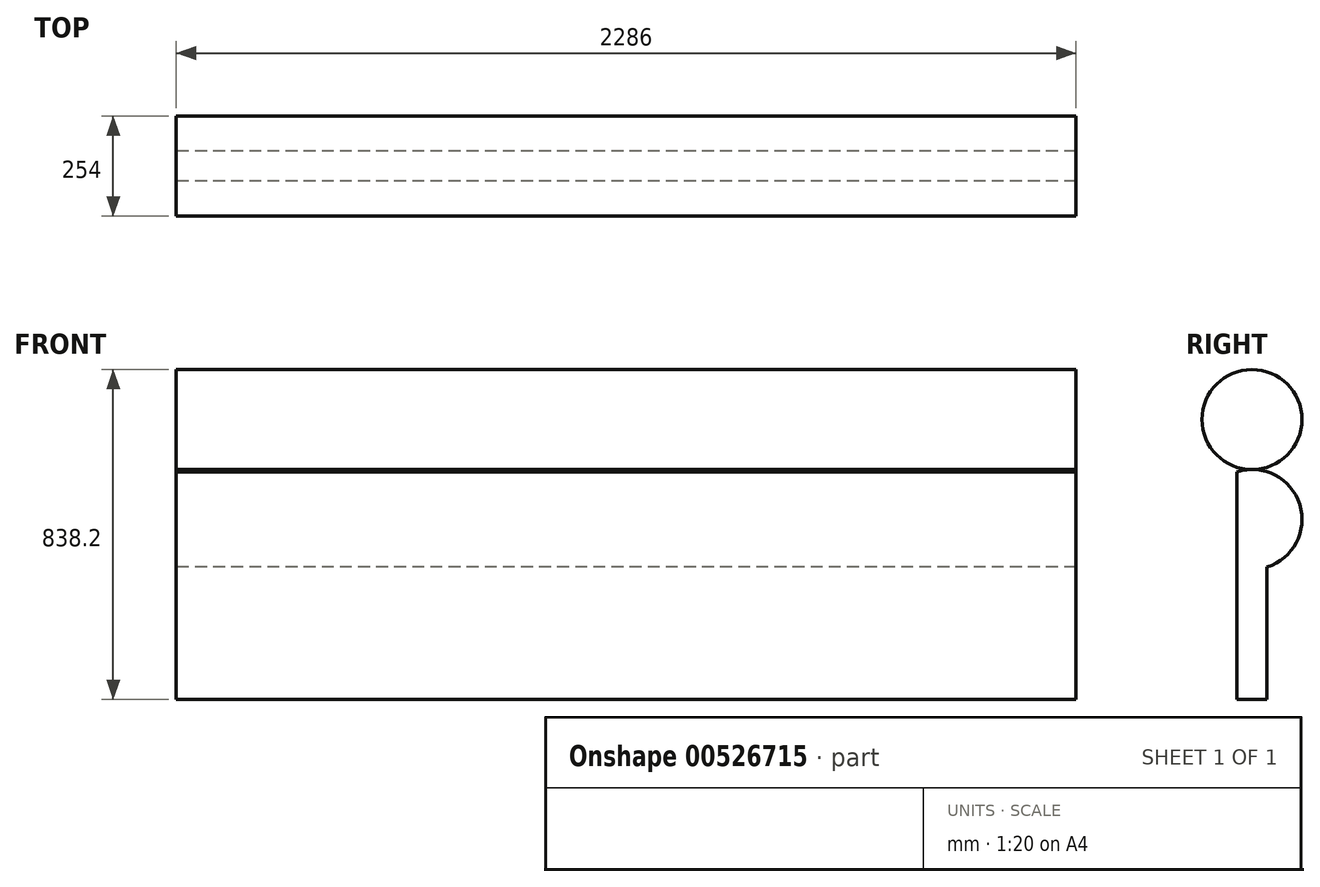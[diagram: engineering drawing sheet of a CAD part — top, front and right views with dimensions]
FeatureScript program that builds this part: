
annotation { "Feature Type Name" : "Feature", "Feature Type Description" : "" }
export const myFeature = defineFeature(function(context is Context, id is Id, definition is map)
    precondition{}
    {
        {
            var Q0;
            Q0=qCreatedBy(makeId("Right.planeOp"),FACE);
            var sketch = newSketch(context, id + "F0", { "sketchPlane" : qUnion([Q0])});
            skCircle(sketch, "E0", {"center": v(0, 457.2) * mm, "radius": 127 * mm});
            skCircle(sketch, "E1", {"center": v(0, 711.2) * mm, "radius": 127 * mm});
            skLineSegment(sketch, "E2", {"start": v(0, 711.2) * mm, "end": v(38.1, 711.2) * mm});
            skLineSegment(sketch, "E3", {"start": v(38.1, 711.2) * mm, "end": v(38.1, 0) * mm});
            skLineSegment(sketch, "E4", {"start": v(38.1, 0) * mm, "end": v(0, 0) * mm});
            skLineSegment(sketch, "E5.MirrorCS", {"start": v(38.1, 1422.4) * mm, "end": v(0, 1422.4) * mm});
            skLineSegment(sketch, "E6.MirrorCS", {"start": v(0, 711.2) * mm, "end": v(-38.1, 711.2) * mm});
            skLineSegment(sketch, "E7.MirrorCS", {"start": v(-38.1, 711.2) * mm, "end": v(-38.1, 0) * mm});
            skLineSegment(sketch, "E8.MirrorCS", {"start": v(-38.1, 0) * mm, "end": v(0, 0) * mm});
            skSolve(sketch);
        }
        {
            var Q0;
            {var subQ0=sQuery(id+"F0.wireOp",EDGE,"E4");Q0=makeQuery(id+"F0.imprint","IMPRINT",FACE,{"disambiguationData":[TD([[makeQuery(id+"F0.imprint","IMPRINT",EDGE,{"derivedFrom":subQ0}),-1.0]])]});}
            var Q1;
            {var subQ0=sQuery(id+"F0.wireOp",EDGE,"E7.MirrorCS");var subQ1=sQuery(id+"F0.wireOp",EDGE,"E0");var subQ2=makeQuery(id+"F0.imprint","INTERSECT",VERTEX,{"disambiguationData":[OD(0.0)],"derivedFrom":[subQ1,subQ0]});Q1=makeQuery(id+"F0.imprint","IMPRINT",FACE,{"disambiguationData":[TD([[makeQuery(id+"F0.imprint","IMPRINT",EDGE,{"disambiguationData":[TD([[subQ2,-1.0]])],"derivedFrom":subQ1}),1.0]])]});}
            var Q2;
            {var subQ1=sQuery(id+"F0.wireOp",EDGE,"E0");var subQ3=sQuery(id+"F0.wireOp",EDGE,"E3");var subQ5=makeQuery(id+"F0.imprint","INTERSECT",VERTEX,{"disambiguationData":[OD(0.0)],"derivedFrom":[subQ1,subQ3]});Q2=makeQuery(id+"F0.imprint","IMPRINT",FACE,{"disambiguationData":[TD([[makeQuery(id+"F0.imprint","IMPRINT",EDGE,{"disambiguationData":[TD([[subQ5,-1.0]])],"derivedFrom":subQ1}),1.0]])]});}
            var Q3;
            {var subQ0=sQuery(id+"F0.wireOp",EDGE,"E3");var subQ1=sQuery(id+"F0.wireOp",EDGE,"E0");var subQ2=makeQuery(id+"F0.imprint","INTERSECT",VERTEX,{"disambiguationData":[OD(0.0)],"derivedFrom":[subQ1,subQ0]});Q3=makeQuery(id+"F0.imprint","IMPRINT",FACE,{"disambiguationData":[TD([[makeQuery(id+"F0.imprint","IMPRINT",EDGE,{"disambiguationData":[TD([[subQ2,1.0]])],"derivedFrom":subQ1}),1.0]])]});}
            var Q4;
            {var subQ2=sQuery(id+"F0.wireOp",EDGE,"E2");Q4=makeQuery(id+"F0.imprint","IMPRINT",FACE,{"disambiguationData":[TD([[makeQuery(id+"F0.imprint","IMPRINT",EDGE,{"derivedFrom":subQ2}),1.0]])]});}
            var Q5;
            {var subQ1=sQuery(id+"F0.wireOp",EDGE,"E2");Q5=makeQuery(id+"F0.imprint","IMPRINT",FACE,{"disambiguationData":[TD([[makeQuery(id+"F0.imprint","IMPRINT",EDGE,{"derivedFrom":subQ1}),-1.0]])]});}
            extrude(context, id + "F1", {"entities" : qUnion([Q0, Q1, Q2, Q3, Q4, Q5]), "depth" : 2286 * mm, "offsetDistance" : 25.4 * mm});
        }
    });
